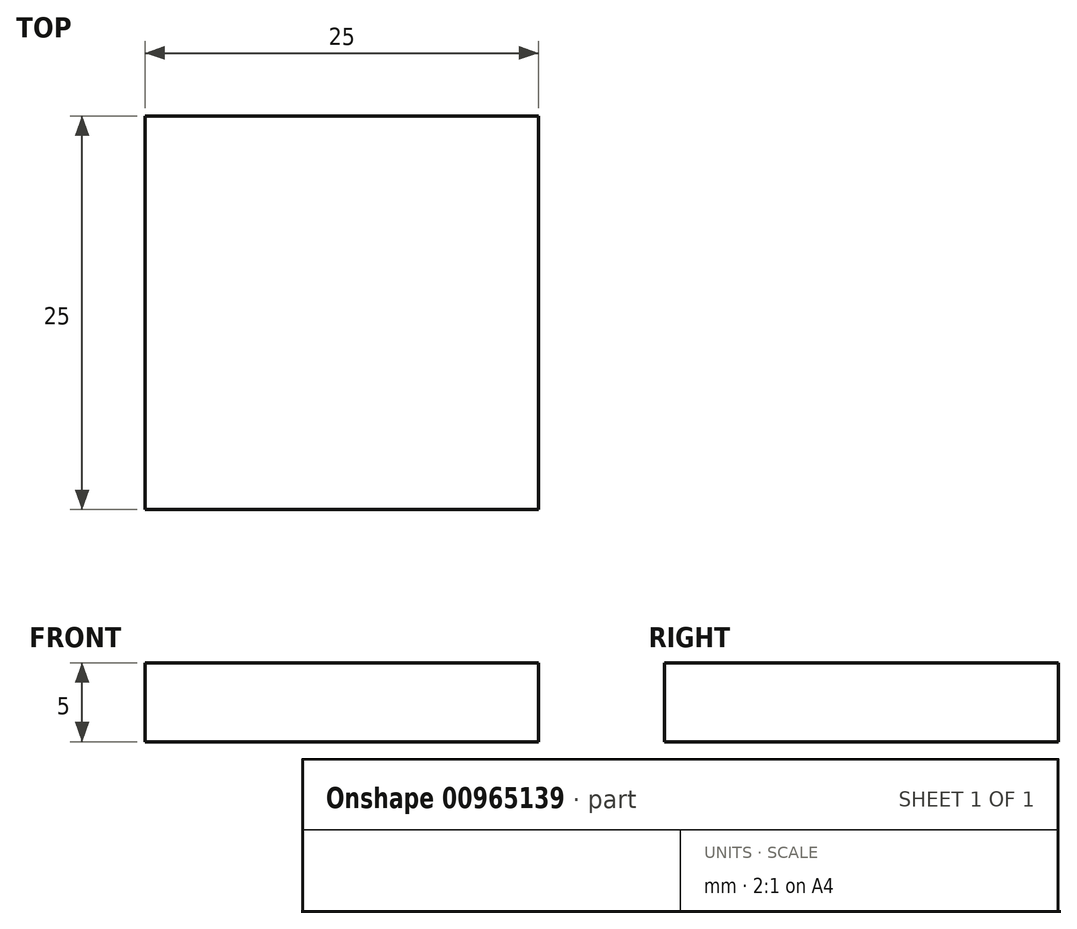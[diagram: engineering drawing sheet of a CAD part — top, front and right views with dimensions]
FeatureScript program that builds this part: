
annotation { "Feature Type Name" : "Feature", "Feature Type Description" : "" }
export const myFeature = defineFeature(function(context is Context, id is Id, definition is map)
    precondition{}
    {
        {
            var Q0;
            Q0=qCreatedBy(makeId("Top.planeOp"),FACE);
            var sketch = newSketch(context, id + "F0", { "sketchPlane" : qUnion([Q0])});
            skLineSegment(sketch, "E0.bottom", {"start": v(-6.61, 18.75) * mm, "end": v(18.39, 18.75) * mm});
            skLineSegment(sketch, "E0.top", {"start": v(-6.61, -6.25) * mm, "end": v(18.39, -6.25) * mm});
            skLineSegment(sketch, "E0.left", {"start": v(-6.61, 18.75) * mm, "end": v(-6.61, -6.25) * mm});
            skLineSegment(sketch, "E0.right", {"start": v(18.39, 18.75) * mm, "end": v(18.39, -6.25) * mm});
            skLineSegment(sketch, "E1.bottom", {"start": v(-6.61, -6.25) * mm, "end": v(-5.16, -6.25) * mm});
            skLineSegment(sketch, "E1.top", {"start": v(-6.61, -6.25) * mm, "end": v(-5.16, -6.25) * mm});
            skLineSegment(sketch, "E1.left", {"start": v(-6.61, -6.25) * mm, "end": v(-6.61, -6.25) * mm});
            skLineSegment(sketch, "E1.right", {"start": v(-5.16, -6.25) * mm, "end": v(-5.16, -6.25) * mm});
            skSolve(sketch);
        }
        {
            var Q0;
            Q0 = qSketchRegion(id + "F0", true);
            extrude(context, id + "F1", {"entities" : qUnion([Q0]), "depth" : 5 * mm, "offsetDistance" : 25 * mm});
        }
    });
